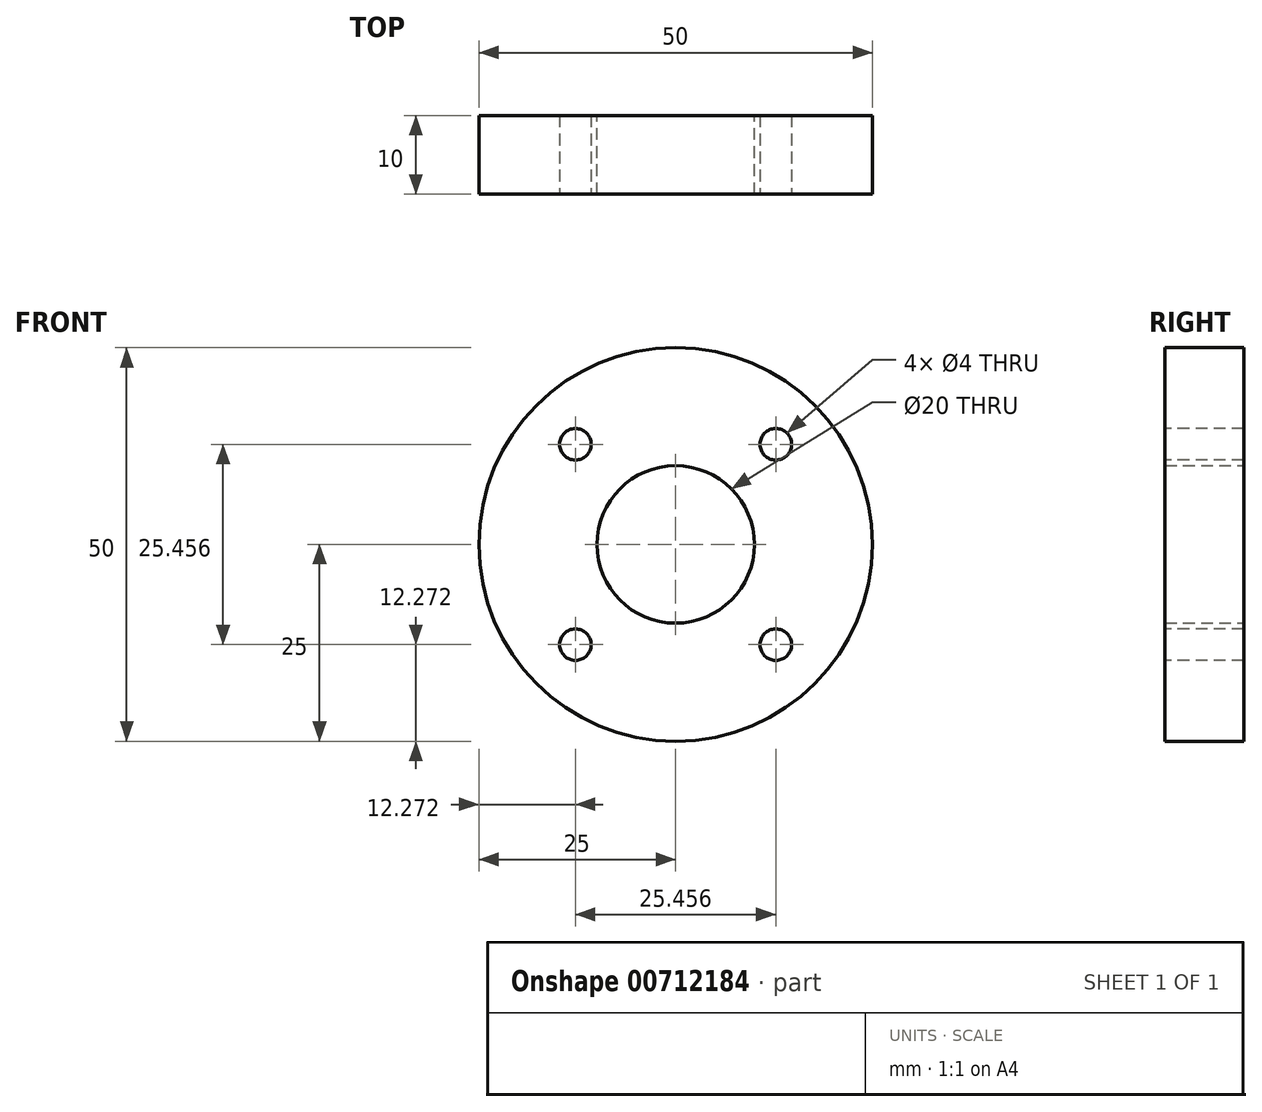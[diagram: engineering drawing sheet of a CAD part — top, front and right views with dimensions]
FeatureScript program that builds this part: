
annotation { "Feature Type Name" : "Feature", "Feature Type Description" : "" }
export const myFeature = defineFeature(function(context is Context, id is Id, definition is map)
    precondition{}
    {
        {
            var Q0;
            Q0=qCreatedBy(makeId("Front.planeOp"),FACE);
            var sketch = newSketch(context, id + "F0", { "sketchPlane" : qUnion([Q0])});
            skCircle(sketch, "E0", {"center": v(0, 0) * mm, "radius": 25 * mm});
            skCircle(sketch, "E1", {"center": v(0, 0) * mm, "radius": 10 * mm});
            skSolve(sketch);
        }
        {
            var Q0;
            Q0 = qSketchRegion(id + "F0", true);
            extrude(context, id + "F1", {"entities" : qUnion([Q0]), "depth" : 10 * mm, "offsetDistance" : 25 * mm});
        }
        {
            var Q0;
            Q0=makeQuery(id+"F1.opExtrude","CAP_FACE",FACE,{"disambiguationData":[OSD([sQuery(id+"F0.wireOp",EDGE,"E0"),sQuery(id+"F0.wireOp",EDGE,"E1")])],"isStart":false});
            var sketch = newSketch(context, id + "F2", { "sketchPlane" : qUnion([Q0])});
            skLineSegment(sketch, "E2", {"start": v(-25, 0) * mm, "end": v(0, 0) * mm, "construction": true});
            skLineSegment(sketch, "E3", {"start": v(0, 0) * mm, "end": v(-17.68, 17.68) * mm, "construction": true});
            skCircle(sketch, "E4", {"center": v(-12.73, 12.73) * mm, "radius": 2 * mm});
            skCircle(sketch, "E5.1.0", {"center": v(-12.73, -12.73) * mm, "radius": 2 * mm});
            skCircle(sketch, "E5.2.0", {"center": v(12.73, -12.73) * mm, "radius": 2 * mm});
            skCircle(sketch, "E5.3.0", {"center": v(12.73, 12.73) * mm, "radius": 2 * mm});
            skPoint(sketch, "E5.center", {"position": v(0, 0) * mm});
            skSolve(sketch);
        }
        {
            var Q0;
            Q0 = qSketchRegion(id + "F2", true);
            extrude(context, id + "F3", {"entities" : qUnion([Q0]), "operationType" : NewBodyOperationType.REMOVE, "endBound" : BoundingType.THROUGH_ALL, "oppositeDirection" : true, "depth" : 25 * mm, "offsetDistance" : 25 * mm});
        }
    });
